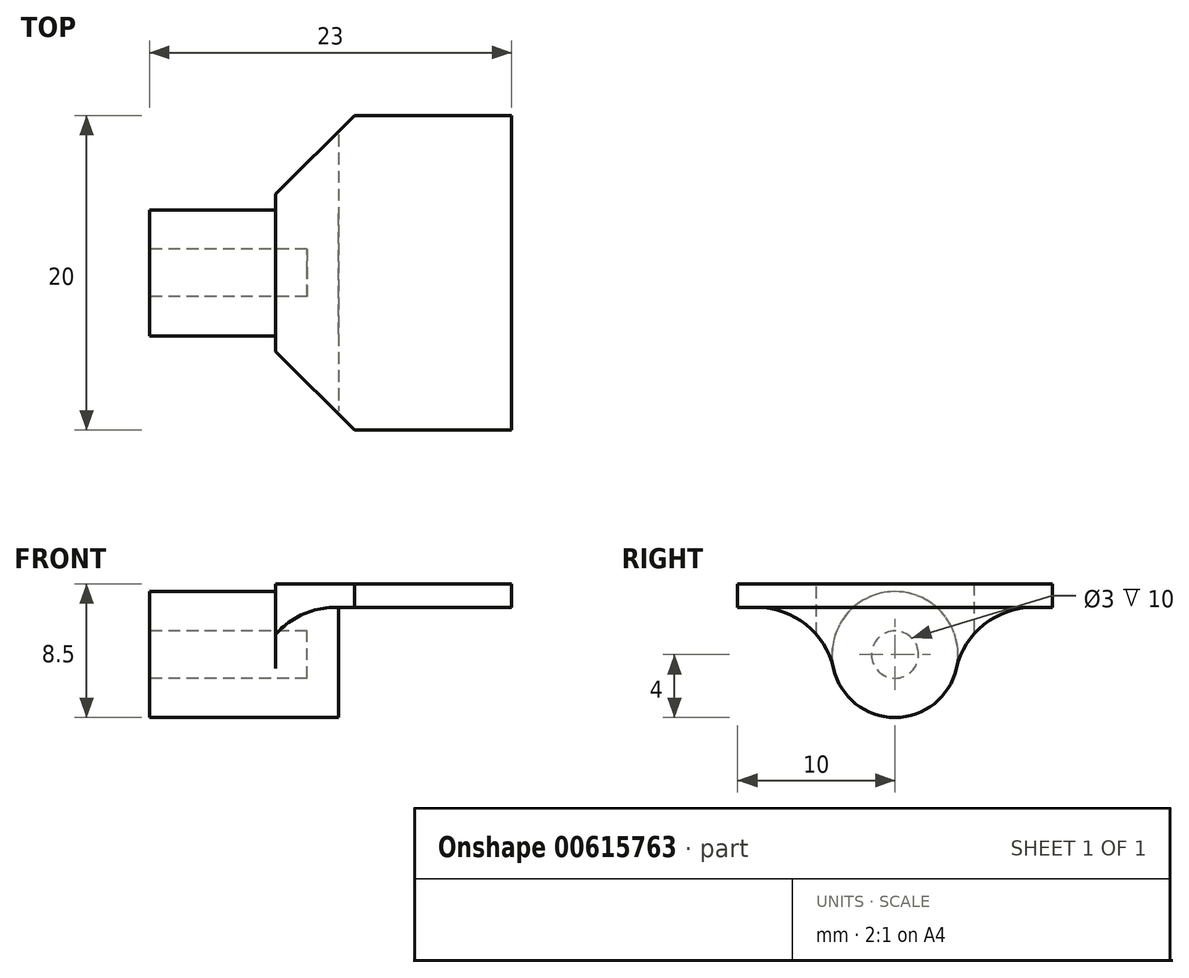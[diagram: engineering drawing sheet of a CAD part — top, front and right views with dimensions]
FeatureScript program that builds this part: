
annotation { "Feature Type Name" : "Feature", "Feature Type Description" : "" }
export const myFeature = defineFeature(function(context is Context, id is Id, definition is map)
    precondition{}
    {
        {
            var Q0;
            Q0=qCreatedBy(makeId("Right.planeOp"),FACE);
            var sketch = newSketch(context, id + "F0", { "sketchPlane" : qUnion([Q0])});
            skCircle(sketch, "E0", {"center": v(0, 0) * mm, "radius": 1.5 * mm});
            skCircle(sketch, "E1", {"center": v(0, 0) * mm, "radius": 4 * mm});
            skSolve(sketch);
        }
        {
            var Q0;
            Q0=makeQuery(id+"F0.imprint","IMPRINT",FACE,{"disambiguationData":[TD([[makeQuery(id+"F0.imprint","IMPRINT",EDGE,{"derivedFrom":sQuery(id+"F0.wireOp",EDGE,"E0")}),-1.0]])]});
            var Q1;
            Q1=qConstructionFilter(qBodyType(qCreatedBy(id+"F0",EDGE),BodyType.WIRE),ConstructionObject.NO);
            extrude(context, id + "F1", {"entities" : qUnion([Q0]), "surfaceEntities" : qUnion([Q1]), "depth" : 10 * mm, "offsetDistance" : 25 * mm});
        }
        {
            var Q0;
            Q0=makeQuery(id+"F1.opExtrude","CAP_FACE",FACE,{"disambiguationData":[OSD([sQuery(id+"F0.wireOp",EDGE,"E0"),sQuery(id+"F0.wireOp",EDGE,"E1")])],"isStart":false});
            var sketch = newSketch(context, id + "F2", { "sketchPlane" : qUnion([Q0])});
            skCircle(sketch, "E2.0", {"center": v(0, 0) * mm, "radius": 4 * mm});
            skSolve(sketch);
        }
        {
            var Q0;
            Q0 = qSketchRegion(id + "F2", true);
            extrude(context, id + "F3", {"entities" : qUnion([Q0]), "operationType" : NewBodyOperationType.ADD, "depth" : 2 * mm, "offsetDistance" : 25 * mm});
        }
        {
            var Q0;
            Q0=qCreatedBy(makeId("Front.planeOp"),FACE);
            var sketch = newSketch(context, id + "F4", { "sketchPlane" : qUnion([Q0])});
            skLineSegment(sketch, "E3", {"start": v(8, 3) * mm, "end": v(23, 3) * mm});
            skLineSegment(sketch, "E4", {"start": v(23, 3) * mm, "end": v(43, 3) * mm});
            skLineSegment(sketch, "E5", {"start": v(8, 3) * mm, "end": v(8, 4.5) * mm});
            skLineSegment(sketch, "E6", {"start": v(8, 4.5) * mm, "end": v(23, 4.5) * mm});
            skLineSegment(sketch, "E7", {"start": v(23, 4.5) * mm, "end": v(23, 3) * mm});
            skSolve(sketch);
        }
        {
            var Q0;
            Q0 = qSketchRegion(id + "F4", true);
            extrude(context, id + "F5", {"entities" : qUnion([Q0]), "operationType" : NewBodyOperationType.ADD, "endBound" : BoundingType.SYMMETRIC, "depth" : 20 * mm, "offsetDistance" : 25 * mm});
        }
        {
            var Q0;
            Q0=makeQuery(id+"F5.boolean.opBoolean","INTERSECT",EDGE,{"disambiguationData":[OD(1.0)],"derivedFrom":[makeQuery(id+"F3.boolean.opBoolean","MERGE",FACE,{"derivedFrom":[makeQuery(id+"F1.opExtrude","SWEPT_FACE",FACE,{"disambiguationData":[OSD([sQuery(id+"F0.wireOp",EDGE,"E1")])]}),makeQuery(id+"F3.opExtrude","SWEPT_FACE",FACE,{"disambiguationData":[OSD([sQuery(id+"F2.wireOp",EDGE,"E2.0")])]})]}),makeQuery(id+"F5.opExtrude","SWEPT_FACE",FACE,{"disambiguationData":[OSD([sQuery(id+"F4.wireOp",EDGE,"E3")])]})]});
            var Q1;
            Q1=makeQuery(id+"F5.boolean.opBoolean","INTERSECT",EDGE,{"disambiguationData":[OD(0.0)],"derivedFrom":[makeQuery(id+"F3.boolean.opBoolean","MERGE",FACE,{"derivedFrom":[makeQuery(id+"F1.opExtrude","SWEPT_FACE",FACE,{"disambiguationData":[OSD([sQuery(id+"F0.wireOp",EDGE,"E1")])]}),makeQuery(id+"F3.opExtrude","SWEPT_FACE",FACE,{"disambiguationData":[OSD([sQuery(id+"F2.wireOp",EDGE,"E2.0")])]})]}),makeQuery(id+"F5.opExtrude","SWEPT_FACE",FACE,{"disambiguationData":[OSD([sQuery(id+"F4.wireOp",EDGE,"E3")])]})]});
            fillet(context, id + "F6", {"entities" : qUnion([Q0, Q1]), "radius" : 5 * mm, "tangentPropagation" : true, "allowEdgeOverflow" : false});
        }
        {
            var Q0;
            Q0=makeQuery(id+"F5.opExtrude","CAP_EDGE",EDGE,{"disambiguationData":[OSD([sQuery(id+"F4.wireOp",EDGE,"E5")])],"isStart":true});
            var Q1;
            Q1=makeQuery(id+"F5.opExtrude","CAP_EDGE",EDGE,{"disambiguationData":[OSD([sQuery(id+"F4.wireOp",EDGE,"E5")])],"isStart":false});
            chamfer(context, id + "F7", {"entities" : qUnion([Q0, Q1]), "width" : 5 * mm, "tangentPropagation" : true});
        }
    });
